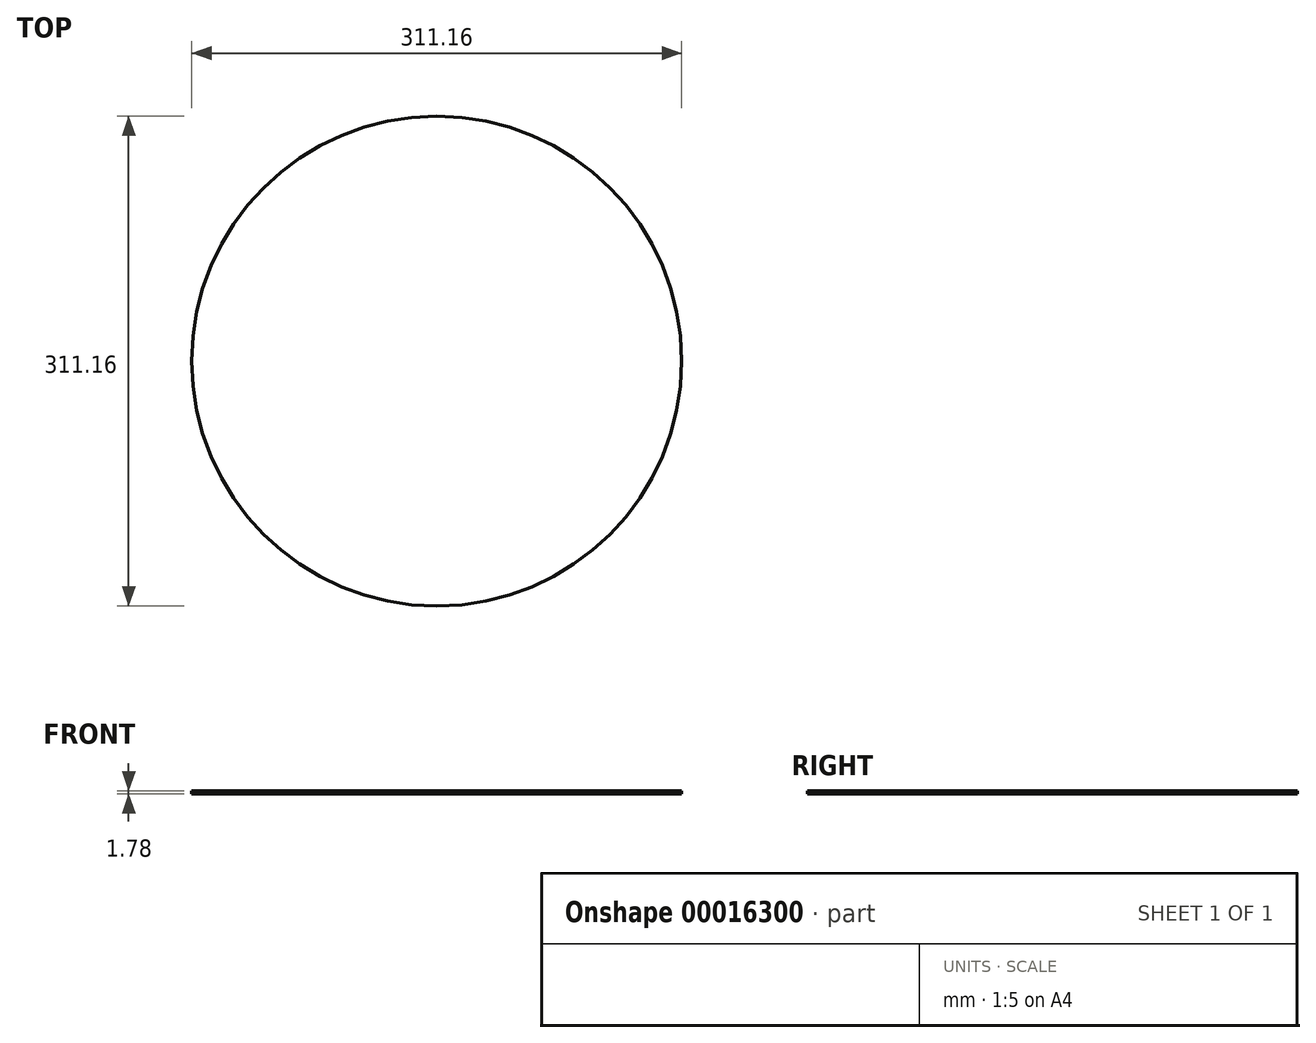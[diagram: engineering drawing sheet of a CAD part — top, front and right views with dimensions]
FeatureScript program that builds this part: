
annotation { "Feature Type Name" : "Feature", "Feature Type Description" : "" }
export const myFeature = defineFeature(function(context is Context, id is Id, definition is map)
    precondition{}
    {
        {
            var Q0;
            Q0=qCreatedBy(makeId("Top.planeOp"),FACE);
            var sketch = newSketch(context, id + "F0", { "sketchPlane" : qUnion([Q0])});
            skCircle(sketch, "E0", {"center": v(0, 0) * mm, "radius": 155.58 * mm});
            skSolve(sketch);
        }
        {
            var Q0;
            Q0 = qSketchRegion(id + "F0", true);
            extrude(context, id + "F1", {"entities" : qUnion([Q0]), "depth" : 1.78 * mm});
        }
    });
